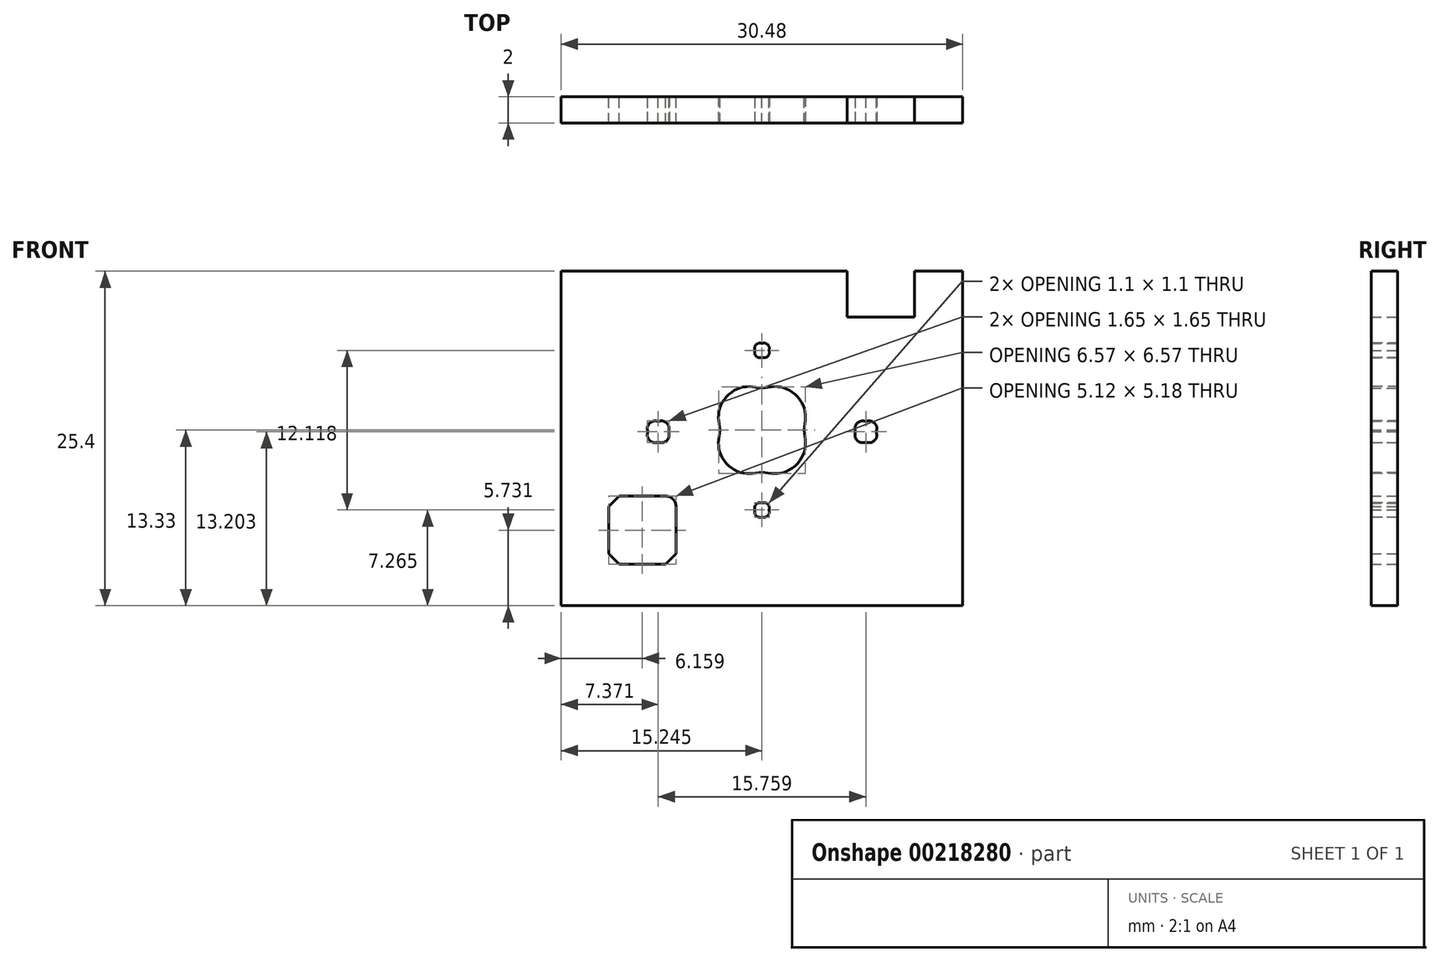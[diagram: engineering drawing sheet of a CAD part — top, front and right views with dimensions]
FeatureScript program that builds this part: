
annotation { "Feature Type Name" : "Feature", "Feature Type Description" : "" }
export const myFeature = defineFeature(function(context is Context, id is Id, definition is map)
    precondition{}
    {
        {
            var Q0;
            Q0=qCreatedBy(makeId("Front.planeOp"),FACE);
            var sketch = newSketch(context, id + "F0", { "sketchPlane" : qUnion([Q0])});
            skLineSegment(sketch, "E0", {"start": v(-15.24, -12.7) * mm, "end": v(-15.24, 12.7) * mm});
            skLineSegment(sketch, "E1", {"start": v(15.24, -12.7) * mm, "end": v(15.24, 12.7) * mm});
            skLineSegment(sketch, "E2", {"start": v(11.59, 12.7) * mm, "end": v(15.24, 12.7) * mm});
            skLineSegment(sketch, "E3", {"start": v(-15.24, 12.7) * mm, "end": v(6.47, 12.7) * mm});
            skLineSegment(sketch, "E4", {"start": v(-15.24, -12.7) * mm, "end": v(15.24, -12.7) * mm});
            skLineSegment(sketch, "E5", {"start": v(6.47, 9.23) * mm, "end": v(6.47, 12.7) * mm});
            skFitSpline(sketch, "E6", {"points": [v(0, -2.55) * mm, v(1.76, -2.55) * mm, v(3.19, -1.13) * mm, v(3.19, 0.63) * mm]});
            skFitSpline(sketch, "E7", {"points": [v(-3.18, 0.63) * mm, v(-3.18, -1.13) * mm, v(-1.75, -2.55) * mm, v(0, -2.55) * mm]});
            skFitSpline(sketch, "E8", {"points": [v(0, 3.81) * mm, v(-1.75, 3.81) * mm, v(-3.18, 2.39) * mm, v(-3.18, 0.63) * mm]});
            skFitSpline(sketch, "E9", {"points": [v(3.19, 0.63) * mm, v(3.19, 2.39) * mm, v(1.76, 3.81) * mm, v(0, 3.81) * mm]});
            skFitSpline(sketch, "E10", {"points": [v(0, -5.97) * mm, v(0.3, -5.97) * mm, v(0.54, -5.73) * mm, v(0.54, -5.43) * mm]});
            skFitSpline(sketch, "E11", {"points": [v(-0.53, -5.43) * mm, v(-0.53, -5.73) * mm, v(-0.29, -5.97) * mm, v(0, -5.97) * mm]});
            skFitSpline(sketch, "E12", {"points": [v(0, -4.9) * mm, v(-0.29, -4.9) * mm, v(-0.53, -5.14) * mm, v(-0.53, -5.43) * mm]});
            skFitSpline(sketch, "E13", {"points": [v(0.54, -5.43) * mm, v(0.54, -5.14) * mm, v(0.3, -4.9) * mm, v(0, -4.9) * mm]});
            skFitSpline(sketch, "E14", {"points": [v(0, 6.15) * mm, v(0.3, 6.15) * mm, v(0.54, 6.39) * mm, v(0.54, 6.68) * mm]});
            skFitSpline(sketch, "E15", {"points": [v(-0.53, 6.68) * mm, v(-0.53, 6.39) * mm, v(-0.29, 6.15) * mm, v(0, 6.15) * mm]});
            skFitSpline(sketch, "E16", {"points": [v(0, 7.22) * mm, v(-0.29, 7.22) * mm, v(-0.53, 6.98) * mm, v(-0.53, 6.68) * mm]});
            skFitSpline(sketch, "E17", {"points": [v(0.54, 6.68) * mm, v(0.54, 6.98) * mm, v(0.3, 7.22) * mm, v(0, 7.22) * mm]});
            skFitSpline(sketch, "E18", {"points": [v(7.89, -0.3) * mm, v(8.33, -0.3) * mm, v(8.69, 0.06) * mm, v(8.69, 0.5) * mm]});
            skFitSpline(sketch, "E19", {"points": [v(7.1, 0.5) * mm, v(7.1, 0.06) * mm, v(7.45, -0.3) * mm, v(7.89, -0.3) * mm]});
            skFitSpline(sketch, "E20", {"points": [v(7.89, 1.3) * mm, v(7.45, 1.3) * mm, v(7.1, 0.94) * mm, v(7.1, 0.5) * mm]});
            skFitSpline(sketch, "E21", {"points": [v(8.69, 0.5) * mm, v(8.69, 0.94) * mm, v(8.33, 1.3) * mm, v(7.89, 1.3) * mm]});
            skFitSpline(sketch, "E22", {"points": [v(-7.87, -0.3) * mm, v(-7.43, -0.3) * mm, v(-7.07, 0.06) * mm, v(-7.07, 0.5) * mm]});
            skFitSpline(sketch, "E23", {"points": [v(-8.67, 0.5) * mm, v(-8.67, 0.06) * mm, v(-8.31, -0.3) * mm, v(-7.87, -0.3) * mm]});
            skFitSpline(sketch, "E24", {"points": [v(-7.87, 1.3) * mm, v(-8.31, 1.3) * mm, v(-8.67, 0.94) * mm, v(-8.67, 0.5) * mm]});
            skFitSpline(sketch, "E25", {"points": [v(-7.07, 0.5) * mm, v(-7.07, 0.94) * mm, v(-7.43, 1.3) * mm, v(-7.87, 1.3) * mm]});
            skLineSegment(sketch, "E26", {"start": v(11.59, 9.23) * mm, "end": v(11.59, 12.7) * mm});
            skLineSegment(sketch, "E27", {"start": v(-10.85, -4.38) * mm, "end": v(-7.31, -4.38) * mm});
            skLineSegment(sketch, "E28", {"start": v(-6.52, -5.18) * mm, "end": v(-6.52, -8.76) * mm});
            skLineSegment(sketch, "E29", {"start": v(-7.31, -9.56) * mm, "end": v(-10.85, -9.56) * mm});
            skLineSegment(sketch, "E30", {"start": v(-11.64, -8.76) * mm, "end": v(-11.64, -5.18) * mm});
            skLineSegment(sketch, "E31", {"start": v(6.47, 9.23) * mm, "end": v(11.59, 9.23) * mm});
            skArc(sketch, "E32", {"start": v(-6.52, -5.18) * mm, "mid": v(-6.75, -4.61) * mm, "end": v(-7.31, -4.38) * mm});
            skLineSegment(sketch, "E33", {"start": v(-7.31, -9.56) * mm, "end": v(-6.52, -8.76) * mm});
            skLineSegment(sketch, "E34", {"start": v(-10.85, -9.56) * mm, "end": v(-11.64, -8.76) * mm});
            skLineSegment(sketch, "E35", {"start": v(-11.64, -5.18) * mm, "end": v(-10.85, -4.38) * mm});
            skSolve(sketch);
        }
        {
            var Q0;
            Q0 = qSketchRegion(id + "F0", true);
            extrude(context, id + "F1", {"entities" : qUnion([Q0]), "depth" : 2 * mm});
        }
    });
